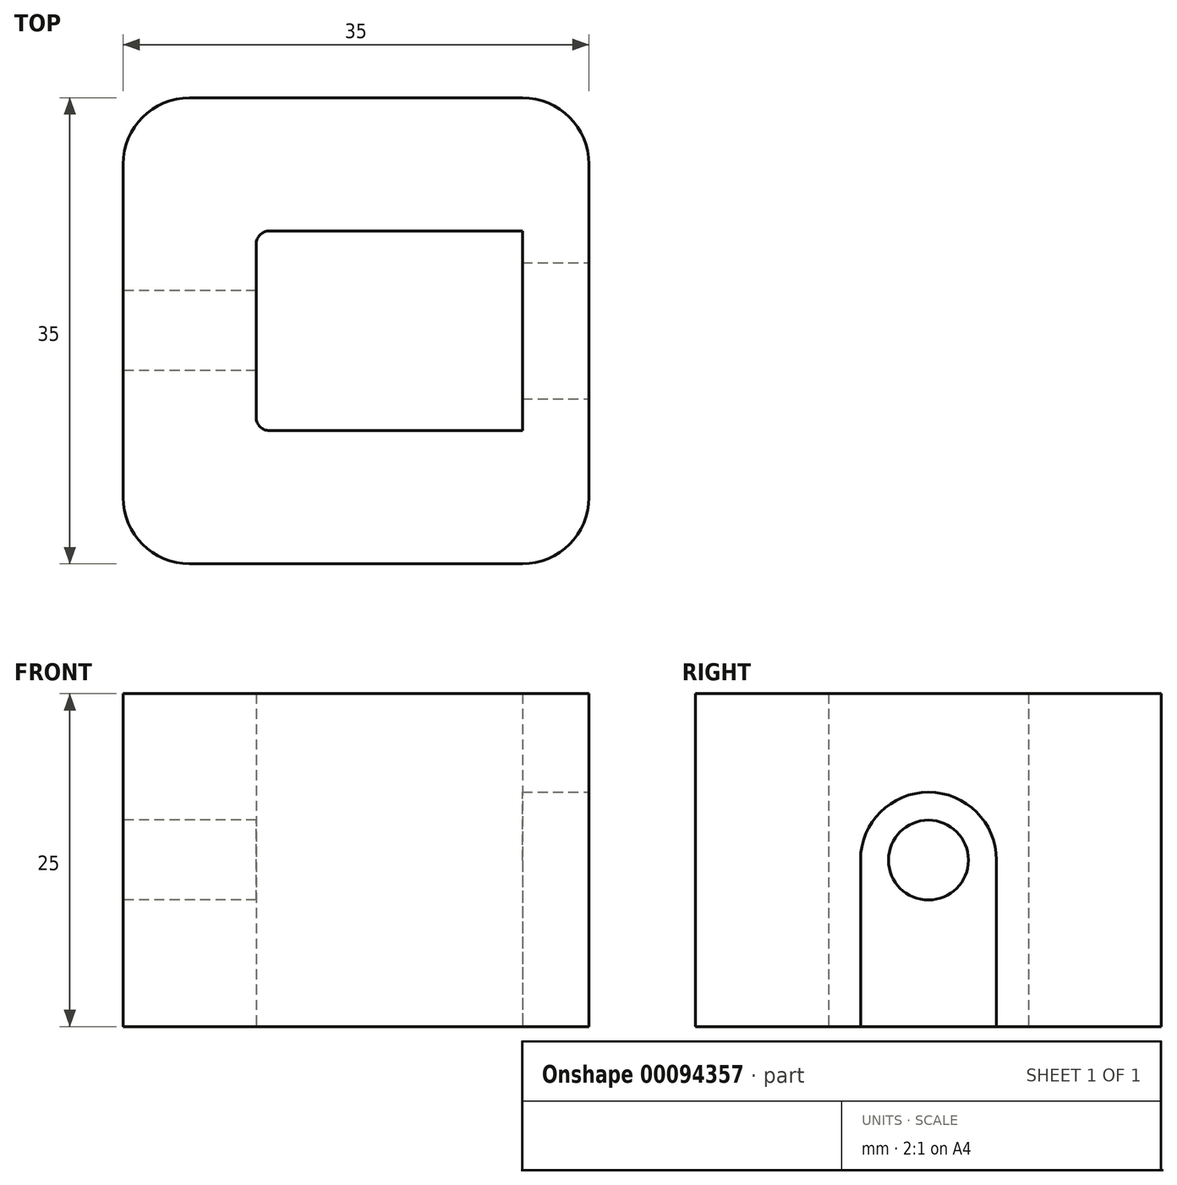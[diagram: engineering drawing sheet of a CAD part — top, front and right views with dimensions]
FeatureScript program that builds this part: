
annotation { "Feature Type Name" : "Feature", "Feature Type Description" : "" }
export const myFeature = defineFeature(function(context is Context, id is Id, definition is map)
    precondition{}
    {
        {
            var Q0;
            Q0=qCreatedBy(makeId("Top.planeOp"),FACE);
            var sketch = newSketch(context, id + "F0", { "sketchPlane" : qUnion([Q0])});
            skLineSegment(sketch, "E0.bottom", {"start": v(15, -7.5) * mm, "end": v(-15, -7.5) * mm});
            skLineSegment(sketch, "E0.top", {"start": v(15, 7.5) * mm, "end": v(-15, 7.5) * mm});
            skLineSegment(sketch, "E0.left", {"start": v(15, -7.5) * mm, "end": v(15, 7.5) * mm});
            skLineSegment(sketch, "E0.right", {"start": v(-15, -7.5) * mm, "end": v(-15, 7.5) * mm});
            skPoint(sketch, "E0.middle", {"position": v(0, 0) * mm});
            skLineSegment(sketch, "E1.bottom", {"start": v(-15, -7.5) * mm, "end": v(15, -7.5) * mm});
            skLineSegment(sketch, "E1.top", {"start": v(-15, -17.5) * mm, "end": v(15, -17.5) * mm});
            skLineSegment(sketch, "E1.left", {"start": v(-15, -7.5) * mm, "end": v(-15, -17.5) * mm});
            skLineSegment(sketch, "E1.right", {"start": v(15, -7.5) * mm, "end": v(15, -17.5) * mm});
            skLineSegment(sketch, "E2.top", {"start": v(15, 17.5) * mm, "end": v(-15, 17.5) * mm});
            skLineSegment(sketch, "E2.left", {"start": v(15, 7.5) * mm, "end": v(15, 17.5) * mm});
            skLineSegment(sketch, "E2.right", {"start": v(-15, 7.5) * mm, "end": v(-15, 17.5) * mm});
            skLineSegment(sketch, "E3.bottom", {"start": v(15, 17.5) * mm, "end": v(20, 17.5) * mm});
            skLineSegment(sketch, "E3.top", {"start": v(15, 5.1) * mm, "end": v(20, 5.1) * mm});
            skLineSegment(sketch, "E3.left", {"start": v(15, 17.5) * mm, "end": v(15, 5.1) * mm});
            skLineSegment(sketch, "E3.right", {"start": v(20, 17.5) * mm, "end": v(20, 5.1) * mm});
            skLineSegment(sketch, "E4.bottom", {"start": v(15, -17.5) * mm, "end": v(20, -17.5) * mm});
            skLineSegment(sketch, "E4.top", {"start": v(15, -5.1) * mm, "end": v(20, -5.1) * mm});
            skLineSegment(sketch, "E4.left", {"start": v(15, -17.5) * mm, "end": v(15, -5.1) * mm});
            skLineSegment(sketch, "E4.right", {"start": v(20, -17.5) * mm, "end": v(20, -5.1) * mm});
            skLineSegment(sketch, "E5", {"start": v(-5, 7.5) * mm, "end": v(-5, -7.5) * mm});
            skLineSegment(sketch, "E6.left", {"start": v(15, 5.1) * mm, "end": v(15, -5.1) * mm});
            skLineSegment(sketch, "E6.right", {"start": v(20, 5.1) * mm, "end": v(20, -5.1) * mm});
            skSolve(sketch);
        }
        {
            var Q0;
            {var subQ1=sQuery(id+"F0.wireOp",EDGE,"E1.top");Q0=makeQuery(id+"F0.imprint","IMPRINT",FACE,{"disambiguationData":[TD([[makeQuery(id+"F0.imprint","IMPRINT",EDGE,{"derivedFrom":subQ1}),1.0]])]});}
            var Q1;
            {var subQ0=sQuery(id+"F0.wireOp",EDGE,"E0.right");Q1=makeQuery(id+"F0.imprint","IMPRINT",FACE,{"disambiguationData":[TD([[makeQuery(id+"F0.imprint","IMPRINT",EDGE,{"derivedFrom":subQ0}),-1.0]])]});}
            var Q2;
            {var subQ1=sQuery(id+"F0.wireOp",EDGE,"E2.top");Q2=makeQuery(id+"F0.imprint","IMPRINT",FACE,{"disambiguationData":[TD([[makeQuery(id+"F0.imprint","IMPRINT",EDGE,{"derivedFrom":subQ1}),1.0]])]});}
            var Q3;
            {var subQ3=sQuery(id+"F0.wireOp",EDGE,"E3.bottom");Q3=makeQuery(id+"F0.imprint","IMPRINT",FACE,{"disambiguationData":[TD([[makeQuery(id+"F0.imprint","IMPRINT",EDGE,{"derivedFrom":subQ3}),-1.0]])]});}
            var Q4;
            Q4=makeQuery(id+"F0.imprint","IMPRINT",FACE,{"disambiguationData":[TD([[makeQuery(id+"F0.imprint","IMPRINT",EDGE,{"derivedFrom":sQuery(id+"F0.wireOp",EDGE,"E3.top")}),-1.0]])]});
            var Q5;
            {var subQ3=sQuery(id+"F0.wireOp",EDGE,"E4.bottom");Q5=makeQuery(id+"F0.imprint","IMPRINT",FACE,{"disambiguationData":[TD([[makeQuery(id+"F0.imprint","IMPRINT",EDGE,{"derivedFrom":subQ3}),1.0]])]});}
            extrude(context, id + "F1", {"entities" : qUnion([Q0, Q1, Q2, Q3, Q4, Q5]), "depth" : 25 * mm});
        }
        {
            var Q0;
            Q0=makeQuery(id+"F1.opExtrude","SWEPT_FACE",FACE,{"disambiguationData":[OSD([sQuery(id+"F0.wireOp",EDGE,"E3.right"),sQuery(id+"F0.wireOp",EDGE,"E4.right"),sQuery(id+"F0.wireOp",EDGE,"E6.right")])]});
            var sketch = newSketch(context, id + "F2", { "sketchPlane" : qUnion([Q0])});
            skPoint(sketch, "E7", {"position": v(0, 12.5) * mm});
            skPoint(sketch, "E7.positionSnap0", {"position": v(17.5, 12.5) * mm});
            skCircle(sketch, "E8", {"center": v(0, 12.5) * mm, "radius": 5.1 * mm});
            skPoint(sketch, "E9.0", {"position": v(5.1, 0) * mm});
            skPoint(sketch, "E9.1", {"position": v(-5.1, 0) * mm});
            skLineSegment(sketch, "E10", {"start": v(5.1, 0) * mm, "end": v(5.1, 12.5) * mm});
            skLineSegment(sketch, "E11", {"start": v(-5.1, 0) * mm, "end": v(-5.1, 12.5) * mm});
            skSolve(sketch);
        }
        {
            var Q0;
            {var subQ0=sQuery(id+"F2.wireOp",EDGE,"E8");var subQ1=makeQuery(id+"F2.imprint","INTERSECT",VERTEX,{"derivedFrom":[subQ0,sQuery(id+"F2.wireOp",EDGE,"E10")]});Q0=makeQuery(id+"F2.imprint","IMPRINT",FACE,{"disambiguationData":[TD([[makeQuery(id+"F2.imprint","IMPRINT",EDGE,{"disambiguationData":[TD([[subQ1,-1.0]])],"derivedFrom":subQ0}),1.0]])]});}
            var Q1;
            {var subQ0=sQuery(id+"F2.wireOp",EDGE,"E10");Q1=makeQuery(id+"F2.imprint","IMPRINT",FACE,{"disambiguationData":[TD([[makeQuery(id+"F2.imprint","IMPRINT",EDGE,{"derivedFrom":subQ0}),1.0]])]});}
            extrude(context, id + "F3", {"entities" : qUnion([Q0, Q1]), "operationType" : NewBodyOperationType.REMOVE, "oppositeDirection" : true, "depth" : 15 * mm});
        }
        {
            var Q0;
            Q0=makeQuery(id+"F1.opExtrude","SWEPT_FACE",FACE,{"disambiguationData":[OSD([sQuery(id+"F0.wireOp",EDGE,"E0.right"),sQuery(id+"F0.wireOp",EDGE,"E1.left"),sQuery(id+"F0.wireOp",EDGE,"E2.right")])]});
            var sketch = newSketch(context, id + "F4", { "sketchPlane" : qUnion([Q0])});
            skCircle(sketch, "E12", {"center": v(0, 12.5) * mm, "radius": 3 * mm});
            skPoint(sketch, "E12.centerSnap0", {"position": v(-17.5, 12.5) * mm});
            skSolve(sketch);
        }
        {
            var Q0;
            Q0=makeQuery(id+"F4.imprint","IMPRINT",FACE,{"disambiguationData":[TD([[makeQuery(id+"F4.imprint","IMPRINT",EDGE,{"derivedFrom":sQuery(id+"F4.wireOp",EDGE,"E12")}),1.0]])]});
            extrude(context, id + "F5", {"entities" : qUnion([Q0]), "operationType" : NewBodyOperationType.REMOVE, "oppositeDirection" : true, "depth" : 25 * mm});
        }
        {
            var Q0;
            Q0=makeQuery(id+"F1.opExtrude","SWEPT_EDGE",EDGE,{"disambiguationData":[OSD([sQuery(id+"F0.wireOp",EDGE,"E1.bottom"),sQuery(id+"F0.wireOp",EDGE,"E4.left")])]});
            var Q1;
            Q1=makeQuery(id+"F1.opExtrude","SWEPT_EDGE",EDGE,{"disambiguationData":[OSD([sQuery(id+"F0.wireOp",EDGE,"E0.top"),sQuery(id+"F0.wireOp",EDGE,"E3.left")])]});
            var Q2;
            Q2=makeQuery(id+"F1.opExtrude","SWEPT_EDGE",EDGE,{"disambiguationData":[OSD([sQuery(id+"F0.wireOp",EDGE,"E1.bottom"),sQuery(id+"F0.wireOp",EDGE,"E5")])]});
            var Q3;
            Q3=makeQuery(id+"F1.opExtrude","SWEPT_EDGE",EDGE,{"disambiguationData":[OSD([sQuery(id+"F0.wireOp",EDGE,"E0.top"),sQuery(id+"F0.wireOp",EDGE,"E5")])]});
            fillet(context, id + "F6", {"entities" : qUnion([Q0, Q1, Q2, Q3]), "radius" : 1 * mm, "tangentPropagation" : true, "allowEdgeOverflow" : false});
        }
        {
            var Q0;
            Q0=makeQuery(id+"F1.opExtrude","SWEPT_EDGE",EDGE,{"disambiguationData":[OSD([sQuery(id+"F0.wireOp",EDGE,"E3.bottom"),sQuery(id+"F0.wireOp",EDGE,"E3.right")])]});
            var Q1;
            Q1=makeQuery(id+"F1.opExtrude","SWEPT_EDGE",EDGE,{"disambiguationData":[OSD([sQuery(id+"F0.wireOp",EDGE,"E4.bottom"),sQuery(id+"F0.wireOp",EDGE,"E4.right")])]});
            var Q2;
            Q2=makeQuery(id+"F1.opExtrude","SWEPT_EDGE",EDGE,{"disambiguationData":[OSD([sQuery(id+"F0.wireOp",EDGE,"E1.top"),sQuery(id+"F0.wireOp",EDGE,"E1.left")])]});
            var Q3;
            Q3=makeQuery(id+"F1.opExtrude","SWEPT_EDGE",EDGE,{"disambiguationData":[OSD([sQuery(id+"F0.wireOp",EDGE,"E2.top"),sQuery(id+"F0.wireOp",EDGE,"E2.right")])]});
            fillet(context, id + "F7", {"entities" : qUnion([Q0, Q1, Q2, Q3]), "radius" : 5 * mm, "tangentPropagation" : true, "allowEdgeOverflow" : false});
        }
    });
